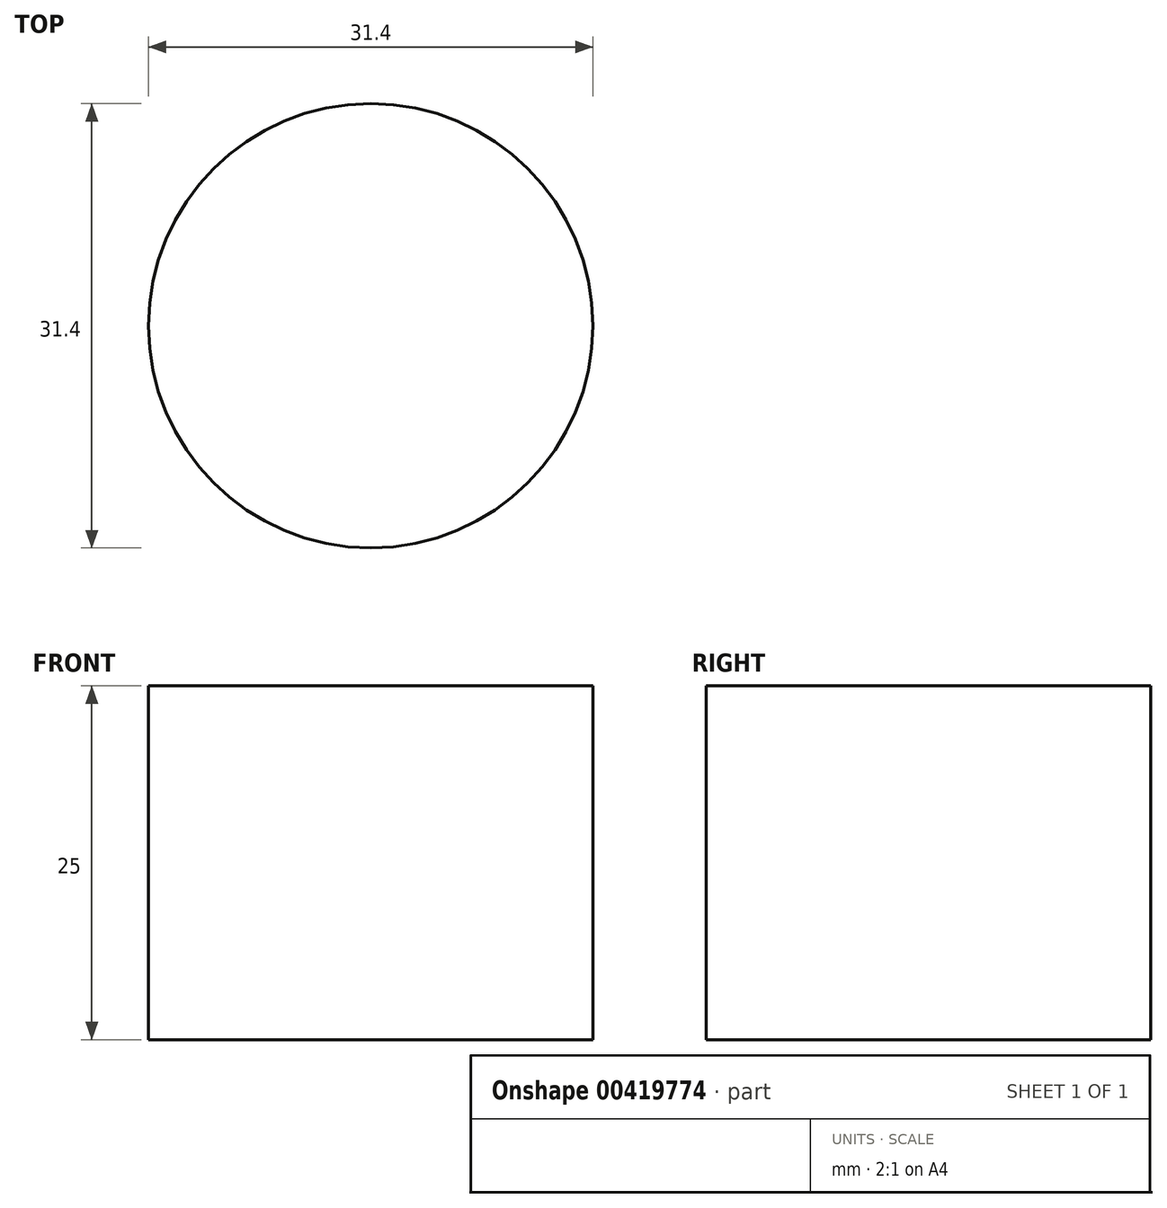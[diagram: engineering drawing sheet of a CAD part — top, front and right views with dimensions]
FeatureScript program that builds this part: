
annotation { "Feature Type Name" : "Feature", "Feature Type Description" : "" }
export const myFeature = defineFeature(function(context is Context, id is Id, definition is map)
    precondition{}
    {
        {
            var Q0;
            Q0=qCreatedBy(makeId("Top.planeOp"),FACE);
            var sketch = newSketch(context, id + "F0", { "sketchPlane" : qUnion([Q0])});
            skCircle(sketch, "E0", {"center": v(0, 0) * mm, "radius": 15.7 * mm});
            skSolve(sketch);
        }
        {
            var Q0;
            Q0=makeQuery(id+"F0.imprint","IMPRINT",FACE,{"disambiguationData":[TD([[makeQuery(id+"F0.imprint","IMPRINT",EDGE,{"derivedFrom":sQuery(id+"F0.wireOp",EDGE,"E0")}),1.0]])]});
            var Q1;
            Q1=sQuery(id+"F0.wireOp",EDGE,"E0");
            var Q2;
            Q2 = qBodyType(qCreatedBy(id + "F0" ,EDGE), BodyType.WIRE);
            extrude(context, id + "F1", {"entities" : qUnion([Q0]), "surfaceEntities" : qUnion([Q1, Q2]), "depth" : 25 * mm});
        }
    });
